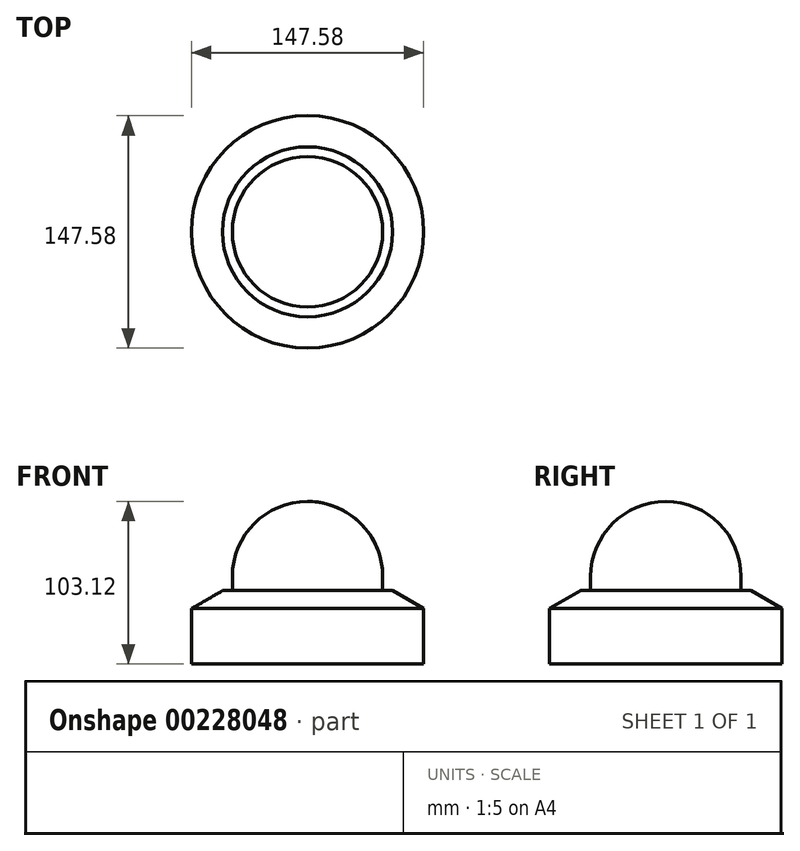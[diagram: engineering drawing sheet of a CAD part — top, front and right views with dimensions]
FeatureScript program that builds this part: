
annotation { "Feature Type Name" : "Feature", "Feature Type Description" : "" }
export const myFeature = defineFeature(function(context is Context, id is Id, definition is map)
    precondition{}
    {
        {
            var Q0;
            Q0=qCreatedBy(makeId("Front.planeOp"),FACE);
            var sketch = newSketch(context, id + "F0", { "sketchPlane" : qUnion([Q0])});
            skLineSegment(sketch, "E0", {"start": v(0, 0) * mm, "end": v(0, 103.12) * mm});
            skLineSegment(sketch, "E1", {"start": v(0, 103.12) * mm, "end": v(0, 103.12) * mm});
            skLineSegment(sketch, "E2", {"start": v(47.75, 55.37) * mm, "end": v(47.75, 46.48) * mm});
            skLineSegment(sketch, "E3", {"start": v(47.75, 46.48) * mm, "end": v(73.79, 46.48) * mm});
            skLineSegment(sketch, "E4", {"start": v(73.79, 46.48) * mm, "end": v(73.79, 0) * mm});
            skLineSegment(sketch, "E5", {"start": v(73.79, 0) * mm, "end": v(0, 0) * mm});
            skPoint(sketch, "E6.visualSharp", {"position": v(47.75, 103.12) * mm});
            skArc(sketch, "E6.filletArc", {"start": v(47.75, 55.37) * mm, "mid": v(33.77, 89.14) * mm, "end": v(0, 103.12) * mm});
            skSolve(sketch);
        }
        {
            var Q0;
            Q0=makeQuery(id+"F0.imprint","IMPRINT",FACE,{"disambiguationData":[TD([[makeQuery(id+"F0.imprint","IMPRINT",EDGE,{"derivedFrom":sQuery(id+"F0.wireOp",EDGE,"E0")}),-1.0]])]});
            var Q1;
            Q1=sQuery(id+"F0.wireOp",EDGE,"E0");
            revolve(context, id + "F1", {"entities" : qUnion([Q0]), "axis" : qUnion([Q1]), "revolveType" : RevolveType.FULL});
        }
        {
            var Q0;
            Q0=makeQuery(id+"F1.opRevolve","SWEPT_EDGE",EDGE,{"disambiguationData":[OSD([sQuery(id+"F0.wireOp",EDGE,"E3"),sQuery(id+"F0.wireOp",EDGE,"E4")])]});
            chamfer(context, id + "F2", {"entities" : qUnion([Q0]), "chamferType" : ChamferType.OFFSET_ANGLE, "width" : 11.43 * mm, "oppositeDirection" : false, "angle" : 60 * degree, "tangentPropagation" : true});
        }
    });
